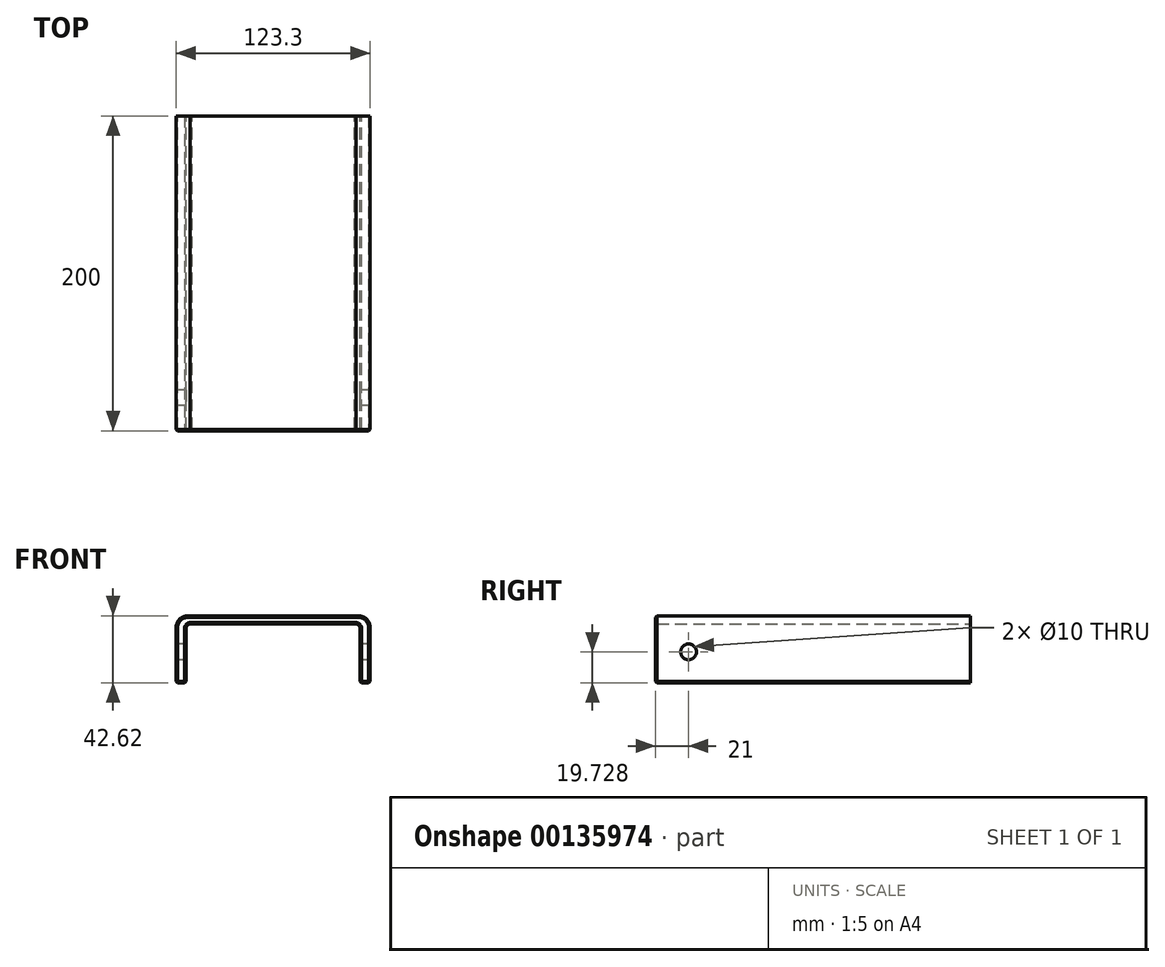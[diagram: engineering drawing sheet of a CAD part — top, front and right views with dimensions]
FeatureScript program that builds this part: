
annotation { "Feature Type Name" : "Feature", "Feature Type Description" : "" }
export const myFeature = defineFeature(function(context is Context, id is Id, definition is map)
    precondition{}
    {
        {
            var Q0;
            Q0=qCreatedBy(makeId("Front.planeOp"),FACE);
            var sketch = newSketch(context, id + "F0", { "sketchPlane" : qUnion([Q0])});
            skLineSegment(sketch, "E0", {"start": v(3.48, 42.5) * mm, "end": v(56.32, 42.5) * mm});
            skLineSegment(sketch, "E1", {"start": v(65.13, 35.13) * mm, "end": v(65.13, 0) * mm});
            skLineSegment(sketch, "E2", {"start": v(65.13, 0) * mm, "end": v(58.78, 0) * mm});
            skLineSegment(sketch, "E3", {"start": v(58.78, 0) * mm, "end": v(58.78, 34.51) * mm});
            skLineSegment(sketch, "E4", {"start": v(55.1, 37.38) * mm, "end": v(3.48, 37.38) * mm});
            skArc(sketch, "E5", {"start": v(65.13, 35.13) * mm, "mid": v(62.45, 40.87) * mm, "end": v(56.32, 42.5) * mm});
            skArc(sketch, "E6", {"start": v(58.78, 34.51) * mm, "mid": v(57.64, 36.85) * mm, "end": v(55.1, 37.38) * mm});
            skLineSegment(sketch, "E7", {"start": v(3.48, 42.5) * mm, "end": v(3.48, 37.38) * mm, "construction": true});
            skLineSegment(sketch, "E8.MirrorCS", {"start": v(-58.17, 0) * mm, "end": v(-51.82, 0) * mm});
            skArc(sketch, "E9.MirrorCS", {"start": v(-58.17, 35.13) * mm, "mid": v(-55.48, 40.87) * mm, "end": v(-49.36, 42.5) * mm});
            skLineSegment(sketch, "E10.MirrorCS", {"start": v(-58.17, 35.13) * mm, "end": v(-58.17, 0) * mm});
            skLineSegment(sketch, "E11.MirrorCS", {"start": v(-51.82, 0) * mm, "end": v(-51.82, 34.51) * mm});
            skLineSegment(sketch, "E12.MirrorCS", {"start": v(3.48, 42.5) * mm, "end": v(-49.36, 42.5) * mm});
            skLineSegment(sketch, "E13.MirrorCS", {"start": v(-48.13, 37.38) * mm, "end": v(3.48, 37.38) * mm});
            skArc(sketch, "E14.MirrorCS", {"start": v(-51.82, 34.51) * mm, "mid": v(-50.68, 36.85) * mm, "end": v(-48.13, 37.38) * mm});
            skSolve(sketch);
        }
        {
            var Q0;
            Q0=makeQuery(id+"F0.imprint","IMPRINT",FACE,{"disambiguationData":[TD([[makeQuery(id+"F0.imprint","IMPRINT",EDGE,{"derivedFrom":sQuery(id+"F0.wireOp",EDGE,"E0")}),-1.0]])]});
            extrude(context, id + "F1", {"entities" : qUnion([Q0]), "depth" : 200 * mm});
        }
        {
            var Q0;
            Q0=makeQuery(id+"F1.opExtrude","CAP_EDGE",EDGE,{"disambiguationData":[OSD([sQuery(id+"F0.wireOp",EDGE,"E0"),sQuery(id+"F0.wireOp",EDGE,"E12.MirrorCS")])],"isStart":false});
            var Q1;
            Q1=makeQuery(id+"F1.opExtrude","CAP_EDGE",EDGE,{"disambiguationData":[OSD([sQuery(id+"F0.wireOp",EDGE,"E4"),sQuery(id+"F0.wireOp",EDGE,"E13.MirrorCS")])],"isStart":false});
            var Q2;
            Q2=makeQuery(id+"F1.opExtrude","CAP_EDGE",EDGE,{"disambiguationData":[OSD([sQuery(id+"F0.wireOp",EDGE,"E9.MirrorCS")])],"isStart":false});
            var Q3;
            Q3=makeQuery(id+"F1.opExtrude","CAP_EDGE",EDGE,{"disambiguationData":[OSD([sQuery(id+"F0.wireOp",EDGE,"E14.MirrorCS")])],"isStart":false});
            var Q4;
            Q4=makeQuery(id+"F1.opExtrude","CAP_EDGE",EDGE,{"disambiguationData":[OSD([sQuery(id+"F0.wireOp",EDGE,"E11.MirrorCS")])],"isStart":false});
            var Q5;
            Q5=makeQuery(id+"F1.opExtrude","CAP_EDGE",EDGE,{"disambiguationData":[OSD([sQuery(id+"F0.wireOp",EDGE,"E10.MirrorCS")])],"isStart":false});
            var Q6;
            Q6=makeQuery(id+"F1.opExtrude","CAP_EDGE",EDGE,{"disambiguationData":[OSD([sQuery(id+"F0.wireOp",EDGE,"E8.MirrorCS")])],"isStart":false});
            var Q7;
            Q7=makeQuery(id+"F1.opExtrude","CAP_EDGE",EDGE,{"disambiguationData":[OSD([sQuery(id+"F0.wireOp",EDGE,"E3")])],"isStart":false});
            var Q8;
            Q8=makeQuery(id+"F1.opExtrude","CAP_EDGE",EDGE,{"disambiguationData":[OSD([sQuery(id+"F0.wireOp",EDGE,"E6")])],"isStart":false});
            var Q9;
            Q9=makeQuery(id+"F1.opExtrude","CAP_EDGE",EDGE,{"disambiguationData":[OSD([sQuery(id+"F0.wireOp",EDGE,"E5")])],"isStart":false});
            var Q10;
            Q10=makeQuery(id+"F1.opExtrude","CAP_EDGE",EDGE,{"disambiguationData":[OSD([sQuery(id+"F0.wireOp",EDGE,"E1")])],"isStart":false});
            var Q11;
            Q11=makeQuery(id+"F1.opExtrude","CAP_EDGE",EDGE,{"disambiguationData":[OSD([sQuery(id+"F0.wireOp",EDGE,"E2")])],"isStart":false});
            var Q12;
            Q12=makeQuery(id+"F1.opExtrude","SWEPT_EDGE",EDGE,{"disambiguationData":[OSD([sQuery(id+"F0.wireOp",EDGE,"E2"),sQuery(id+"F0.wireOp",EDGE,"E3")])]});
            var Q13;
            Q13=makeQuery(id+"F1.opExtrude","SWEPT_EDGE",EDGE,{"disambiguationData":[OSD([sQuery(id+"F0.wireOp",EDGE,"E1"),sQuery(id+"F0.wireOp",EDGE,"E2")])]});
            var Q14;
            Q14=makeQuery(id+"F1.opExtrude","SWEPT_EDGE",EDGE,{"disambiguationData":[OSD([sQuery(id+"F0.wireOp",EDGE,"E8.MirrorCS"),sQuery(id+"F0.wireOp",EDGE,"E11.MirrorCS")])]});
            var Q15;
            Q15=makeQuery(id+"F1.opExtrude","SWEPT_EDGE",EDGE,{"disambiguationData":[OSD([sQuery(id+"F0.wireOp",EDGE,"E8.MirrorCS"),sQuery(id+"F0.wireOp",EDGE,"E10.MirrorCS")])]});
            chamfer(context, id + "F2", {"entities" : qUnion([Q0, Q1, Q2, Q3, Q4, Q5, Q6, Q7, Q8, Q9, Q10, Q11, Q12, Q13, Q14, Q15]), "width" : 1 * mm, "tangentPropagation" : true});
        }
        {
            var Q0;
            Q0=makeQuery(id+"F1.opExtrude","SWEPT_FACE",FACE,{"disambiguationData":[OSD([sQuery(id+"F0.wireOp",EDGE,"E10.MirrorCS")])]});
            var sketch = newSketch(context, id + "F3", { "sketchPlane" : qUnion([Q0])});
            skCircle(sketch, "E15", {"center": v(179, 19.73) * mm, "radius": 5 * mm});
            skSolve(sketch);
        }
        {
            var Q0;
            Q0=makeQuery(id+"F3.imprint","IMPRINT",FACE,{"disambiguationData":[TD([[makeQuery(id+"F3.imprint","IMPRINT",EDGE,{"derivedFrom":sQuery(id+"F3.wireOp",EDGE,"E15")}),1.0]])]});
            extrude(context, id + "F4", {"entities" : qUnion([Q0]), "operationType" : NewBodyOperationType.REMOVE, "endBound" : BoundingType.THROUGH_ALL, "oppositeDirection" : true, "depth" : 140.9 * mm});
        }
    });
